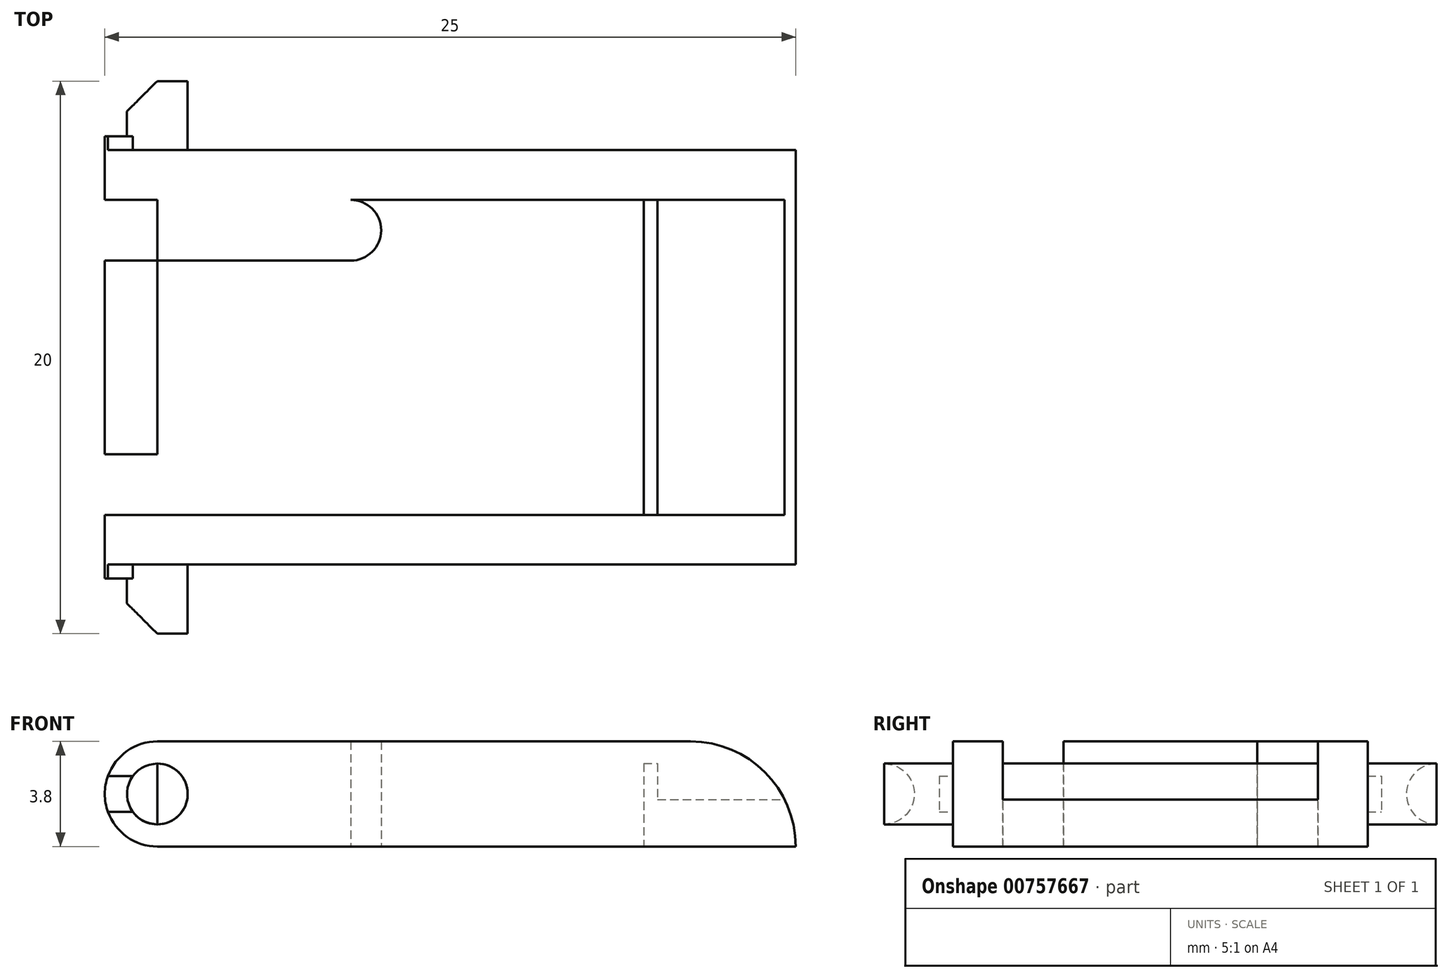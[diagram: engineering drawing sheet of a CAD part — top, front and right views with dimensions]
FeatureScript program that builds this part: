
annotation { "Feature Type Name" : "Feature", "Feature Type Description" : "" }
export const myFeature = defineFeature(function(context is Context, id is Id, definition is map)
    precondition{}
    {
        {
            var Q0;
            Q0=qCreatedBy(makeId("Front.planeOp"),FACE);
            var sketch = newSketch(context, id + "F0", { "sketchPlane" : qUnion([Q0])});
            skLineSegment(sketch, "E0.left", {"start": v(0, 0) * mm, "end": v(23.1, 0) * mm});
            skLineSegment(sketch, "E0.right", {"start": v(0, 3.8) * mm, "end": v(19.3, 3.8) * mm});
            skPoint(sketch, "E0.middle", {"position": v(0, 0) * mm});
            skLineSegment(sketch, "E1", {"start": v(0, 0) * mm, "end": v(0, 3.8) * mm, "construction": true});
            skCircle(sketch, "E2", {"center": v(0, 1.9) * mm, "radius": 1.9 * mm});
            skCircle(sketch, "E3", {"center": v(0, 1.9) * mm, "radius": 1.1 * mm});
            skLineSegment(sketch, "E4", {"start": v(-1.9, 1.9) * mm, "end": v(1.9, 1.9) * mm, "construction": true});
            skLineSegment(sketch, "E5", {"start": v(-1.79, 1.25) * mm, "end": v(-0.89, 1.25) * mm});
            skLineSegment(sketch, "E6.MirrorCS", {"start": v(-1.79, 2.55) * mm, "end": v(-0.89, 2.55) * mm});
            skPoint(sketch, "E7", {"position": v(-1.9, 1.9) * mm});
            skArc(sketch, "E8", {"start": v(23.1, 0) * mm, "mid": v(21.99, 2.69) * mm, "end": v(19.3, 3.8) * mm});
            skLineSegment(sketch, "E9", {"start": v(-1.9, 5.35) * mm, "end": v(-1.9, -2.79) * mm, "construction": true});
            skLineSegment(sketch, "E10", {"start": v(23.1, 4.6) * mm, "end": v(23.1, -3.54) * mm, "construction": true});
            skSolve(sketch);
        }
        {
            var Q0;
            Q0 = qSketchRegion(id + "F0", true);
            extrude(context, id + "F1", {"entities" : qUnion([Q0]), "endBound" : BoundingType.SYMMETRIC, "depth" : 15 * mm, "offsetDistance" : 25 * mm});
        }
        {
            var Q0;
            {var subQ0=sQuery(id+"F0.wireOp",EDGE,"E3");var subQ1=makeQuery(id+"F0.imprint","INTERSECT",VERTEX,{"derivedFrom":[subQ0,sQuery(id+"F0.wireOp",EDGE,"E5")]});Q0=makeQuery(id+"F0.imprint","IMPRINT",FACE,{"disambiguationData":[TD([[makeQuery(id+"F0.imprint","IMPRINT",EDGE,{"disambiguationData":[TD([[subQ1,1.0]])],"derivedFrom":subQ0}),1.0]])]});}
            extrude(context, id + "F2", {"entities" : qUnion([Q0]), "operationType" : NewBodyOperationType.ADD, "endBound" : BoundingType.SYMMETRIC, "depth" : 20 * mm, "offsetDistance" : 25 * mm});
        }
        {
            var Q0;
            {var subQ0=sQuery(id+"F0.wireOp",EDGE,"E5");Q0=makeQuery(id+"F0.imprint","IMPRINT",FACE,{"disambiguationData":[TD([[makeQuery(id+"F0.imprint","IMPRINT",EDGE,{"derivedFrom":subQ0}),1.0]])]});}
            extrude(context, id + "F3", {"entities" : qUnion([Q0]), "operationType" : NewBodyOperationType.ADD, "endBound" : BoundingType.SYMMETRIC, "depth" : 16 * mm, "offsetDistance" : 25 * mm});
        }
        {
            var Q0;
            Q0=qCreatedBy(makeId("Top.planeOp"),FACE);
            var sketch = newSketch(context, id + "F4", { "sketchPlane" : qUnion([Q0])});
            skLineSegment(sketch, "E11", {"start": v(-1.9, -5.7) * mm, "end": v(7, -5.7) * mm});
            skLineSegment(sketch, "E12", {"start": v(-1.9, -7.5) * mm, "end": v(-1.9, 7.5) * mm, "construction": true});
            skLineSegment(sketch, "E13.0", {"start": v(-1.9, -7.5) * mm, "end": v(0, -7.5) * mm, "construction": true});
            skPoint(sketch, "E14.orphan", {"position": v(0, -7.5) * mm});
            skLineSegment(sketch, "E15.0", {"start": v(-1.9, 7.5) * mm, "end": v(0, 7.5) * mm, "construction": true});
            skPoint(sketch, "E16.orphan", {"position": v(0, 7.5) * mm});
            skLineSegment(sketch, "E17", {"start": v(0, 7.5) * mm, "end": v(0, -10) * mm, "construction": true});
            skLineSegment(sketch, "E18", {"start": v(-1.9, -4.6) * mm, "end": v(0, -4.6) * mm, "construction": true});
            skLineSegment(sketch, "E19.MirrorCS", {"start": v(-1.9, -3.5) * mm, "end": v(7, -3.5) * mm});
            skArc(sketch, "E20", {"start": v(7, -5.7) * mm, "mid": v(8.1, -4.6) * mm, "end": v(7, -3.5) * mm});
            skLineSegment(sketch, "E21.MirrorCS", {"start": v(-1.9, 3.5) * mm, "end": v(7, 3.5) * mm});
            skArc(sketch, "E22.MirrorCS", {"start": v(7, 5.7) * mm, "mid": v(8.1, 4.6) * mm, "end": v(7, 3.5) * mm});
            skLineSegment(sketch, "E23.MirrorCS", {"start": v(-1.9, 5.7) * mm, "end": v(7, 5.7) * mm});
            skLineSegment(sketch, "E24", {"start": v(-1.9, -3.5) * mm, "end": v(-1.9, -5.7) * mm});
            skLineSegment(sketch, "E25.MirrorCS", {"start": v(-1.9, 3.5) * mm, "end": v(-1.9, 5.7) * mm});
            skLineSegment(sketch, "E26.bottom", {"start": v(0, -5.7) * mm, "end": v(23.1, -5.7) * mm});
            skLineSegment(sketch, "E26.top", {"start": v(0, 5.7) * mm, "end": v(23.1, 5.7) * mm});
            skLineSegment(sketch, "E26.left", {"start": v(0, -5.7) * mm, "end": v(0, 5.7) * mm});
            skLineSegment(sketch, "E26.right", {"start": v(23.1, -5.7) * mm, "end": v(23.1, 5.7) * mm});
            skLineSegment(sketch, "E27.bottom", {"start": v(17.6, -5.7) * mm, "end": v(18.1, -5.7) * mm});
            skLineSegment(sketch, "E27.top", {"start": v(17.6, 5.7) * mm, "end": v(18.1, 5.7) * mm});
            skLineSegment(sketch, "E27.left", {"start": v(17.6, -5.7) * mm, "end": v(17.6, 5.7) * mm});
            skLineSegment(sketch, "E27.right", {"start": v(18.1, -5.7) * mm, "end": v(18.1, 5.7) * mm});
            skLineSegment(sketch, "E28.0", {"start": v(23.1, -7.5) * mm, "end": v(23.1, 7.5) * mm, "construction": true});
            skLineSegment(sketch, "E29", {"start": v(-1.1, -8.9) * mm, "end": v(-1.1, -10) * mm});
            skLineSegment(sketch, "E30", {"start": v(-1.1, -10) * mm, "end": v(0, -10) * mm});
            skLineSegment(sketch, "E31", {"start": v(0, -10) * mm, "end": v(-1.1, -8.9) * mm});
            skLineSegment(sketch, "E32.0", {"start": v(1.1, -10) * mm, "end": v(-1.1, -10) * mm, "construction": true});
            skLineSegment(sketch, "E33", {"start": v(-1.1, -10.5) * mm, "end": v(-1.1, -8.5) * mm, "construction": true});
            skLineSegment(sketch, "E34.MirrorCS", {"start": v(0, 10) * mm, "end": v(-1.1, 8.9) * mm});
            skLineSegment(sketch, "E35.MirrorCS", {"start": v(-1.1, 8.9) * mm, "end": v(-1.1, 10) * mm});
            skLineSegment(sketch, "E36.MirrorCS", {"start": v(-1.1, 10) * mm, "end": v(0, 10) * mm});
            skSolve(sketch);
        }
        {
            var Q0;
            {var subQ3=sQuery(id+"F4.wireOp",EDGE,"E22.MirrorCS");var subQ7=sQuery(id+"F4.wireOp",EDGE,"E25.MirrorCS");Q0=qUnion([makeQuery(id+"F4.imprint","IMPRINT",FACE,{"disambiguationData":[TD([[makeQuery(id+"F4.imprint","IMPRINT",EDGE,{"derivedFrom":subQ7}),-1.0]])]}),makeQuery(id+"F4.imprint","IMPRINT",FACE,{"disambiguationData":[TD([[makeQuery(id+"F4.imprint","IMPRINT",EDGE,{"derivedFrom":subQ3}),-1.0]])]})]);}
            var Q1;
            {var subQ3=sQuery(id+"F4.wireOp",EDGE,"E24");Q1=makeQuery(id+"F4.imprint","IMPRINT",FACE,{"disambiguationData":[TD([[makeQuery(id+"F4.imprint","IMPRINT",EDGE,{"derivedFrom":subQ3}),1.0]])]});}
            var Q2;
            {var subQ3=sQuery(id+"F4.wireOp",EDGE,"E20");Q2=makeQuery(id+"F4.imprint","IMPRINT",FACE,{"disambiguationData":[TD([[makeQuery(id+"F4.imprint","IMPRINT",EDGE,{"derivedFrom":subQ3}),1.0]])]});}
            extrude(context, id + "F5", {"entities" : qUnion([Q0, Q1, Q2]), "operationType" : NewBodyOperationType.REMOVE, "endBound" : BoundingType.THROUGH_ALL, "depth" : 25 * mm, "offsetDistance" : 25 * mm});
        }
        {
            var Q0;
            {var subQ4=sQuery(id+"F4.wireOp",EDGE,"E20");Q0=makeQuery(id+"F4.imprint","IMPRINT",FACE,{"disambiguationData":[TD([[makeQuery(id+"F4.imprint","IMPRINT",EDGE,{"derivedFrom":subQ4}),-1.0]])]});}
            var Q1;
            {var subQ2=sQuery(id+"F4.wireOp",EDGE,"E26.right");Q1=makeQuery(id+"F4.imprint","IMPRINT",FACE,{"disambiguationData":[TD([[makeQuery(id+"F4.imprint","IMPRINT",EDGE,{"derivedFrom":subQ2}),1.0]])]});}
            extrude(context, id + "F6", {"entities" : qUnion([Q0, Q1]), "operationType" : NewBodyOperationType.REMOVE, "endBound" : BoundingType.THROUGH_ALL, "depth" : 10 * mm, "offsetDistance" : 25 * mm, "hasSecondDirection" : true, "secondDirectionOppositeDirection" : false, "secondDirectionDepth" : (3.8 - 2.1) * mm});
        }
        {
            var Q0;
            {var subQ2=sQuery(id+"F4.wireOp",EDGE,"E27.left");Q0=makeQuery(id+"F4.imprint","IMPRINT",FACE,{"disambiguationData":[TD([[makeQuery(id+"F4.imprint","IMPRINT",EDGE,{"derivedFrom":subQ2}),-1.0]])]});}
            var Q1;
            Q1=makeQuery(id+"F1.opExtrude","SWEPT_FACE",FACE,{"disambiguationData":[OSD([sQuery(id+"F0.wireOp",EDGE,"E0.right")])]});
            extrude(context, id + "F7", {"entities" : qUnion([Q0]), "operationType" : NewBodyOperationType.REMOVE, "endBound" : BoundingType.UP_TO_SURFACE, "depth" : 2 * mm, "endBoundEntityFace" : qUnion([Q1]), "offsetDistance" : 25 * mm, "hasSecondDirection" : true, "secondDirectionOppositeDirection" : false, "secondDirectionDepth" : 3 * mm});
        }
        {
            var Q0;
            Q0=makeQuery(id+"F4.imprint","IMPRINT",FACE,{"disambiguationData":[TD([[makeQuery(id+"F4.imprint","IMPRINT",EDGE,{"derivedFrom":sQuery(id+"F4.wireOp",EDGE,"E34.MirrorCS")}),-1.0]])]});
            var Q1;
            Q1=makeQuery(id+"F4.imprint","IMPRINT",FACE,{"disambiguationData":[TD([[makeQuery(id+"F4.imprint","IMPRINT",EDGE,{"derivedFrom":sQuery(id+"F4.wireOp",EDGE,"E29")}),1.0]])]});
            extrude(context, id + "F8", {"entities" : qUnion([Q0, Q1]), "operationType" : NewBodyOperationType.REMOVE, "depth" : 25 * mm, "offsetDistance" : 25 * mm});
        }
    });
